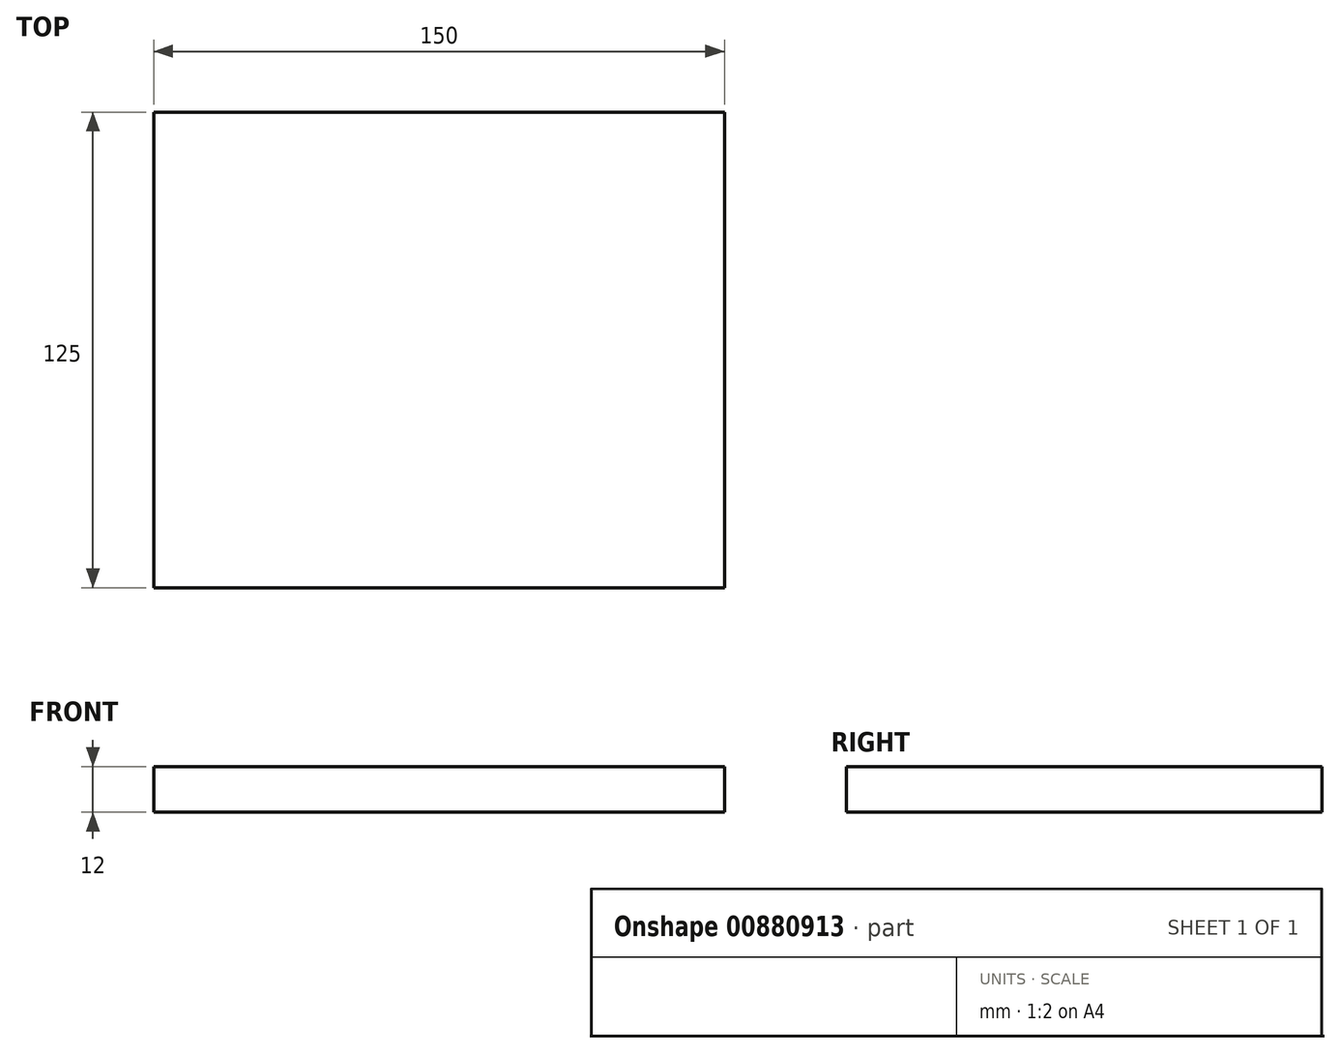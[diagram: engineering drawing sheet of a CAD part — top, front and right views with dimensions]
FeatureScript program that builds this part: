
annotation { "Feature Type Name" : "Feature", "Feature Type Description" : "" }
export const myFeature = defineFeature(function(context is Context, id is Id, definition is map)
    precondition{}
    {
        {
            var Q0;
            Q0=qCreatedBy(makeId("Top.planeOp"),FACE);
            var sketch = newSketch(context, id + "F0", { "sketchPlane" : qUnion([Q0])});
            skLineSegment(sketch, "E0.bottom", {"start": v(-75, 62.5) * mm, "end": v(75, 62.5) * mm});
            skLineSegment(sketch, "E0.top", {"start": v(-75, -62.5) * mm, "end": v(75, -62.5) * mm});
            skLineSegment(sketch, "E0.left", {"start": v(-75, 62.5) * mm, "end": v(-75, -62.5) * mm});
            skLineSegment(sketch, "E0.right", {"start": v(75, 62.5) * mm, "end": v(75, -62.5) * mm});
            skPoint(sketch, "E0.middle", {"position": v(0, 0) * mm});
            skSolve(sketch);
        }
        {
            var Q0;
            Q0=makeQuery(id+"F0.imprint","IMPRINT",FACE,{"disambiguationData":[TD([[makeQuery(id+"F0.imprint","IMPRINT",EDGE,{"derivedFrom":sQuery(id+"F0.wireOp",EDGE,"E0.bottom")}),-1.0]])]});
            extrude(context, id + "F1", {"entities" : qUnion([Q0]), "depth" : 12 * mm, "offsetDistance" : 25 * mm});
        }
    });
